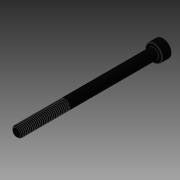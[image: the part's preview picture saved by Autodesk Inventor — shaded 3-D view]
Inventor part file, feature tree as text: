
AUTODESK INVENTOR PART (.ipt)
format: ipt  version: 2014 SP1 (Build 180222100, 222)  size: 689,152 bytes
history: native  units: in
note: dims shown in document units (in); Inventor stores cm internally (conversion verified against a paired STEP export)
features: chamfer x1, other x1, imported_body x1
ambient origin geometry x8: Origin, YZ Plane, XZ Plane, XY Plane, X Axis, Y Axis, Z Axis, Center Point
bodies: Body1 (feature_tree)
feature tree (3):
  chamfer  "Chamfer2"  [1 undecoded]
  other  "91251A3551"
  imported_body  "Base1"
note: 1 required parameter value undecoded (feature->parameter linkage not recoverable at this tier; creation-order binding heuristic only, values carry confidence <= 0.55)
